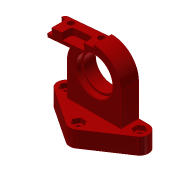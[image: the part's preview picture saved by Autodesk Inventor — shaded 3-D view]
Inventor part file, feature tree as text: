
AUTODESK INVENTOR PART (.ipt)
format: ipt  version: 2015 SP2 (Build 190223200, 223)  size: 307,712 bytes
history: native  units: mm
features: extrude x9, sketch x9, hole x4, projected_geometry x3, fillet x2, other x1, plane x1, chamfer x1
ambient origin geometry x8: Origin, YZ Plane, XZ Plane, XY Plane, X Axis, Y Axis, Z Axis, Center Point
bodies: Body1 (feature_tree)
feature tree (30):
  other  "Sólido1"
  extrude  "Extrusión1"  Depth=5.5mm
  hole  "Agujero1"  [1 undecoded]
  hole  "Agujero2"  [1 undecoded]
  hole  "Agujero3"  [1 undecoded]
  extrude  "Extrusión2"  Depth=10.0mm
  extrude  "Extrusión3"  Depth=6.235mm
  fillet  "Empalme1"  Radius=6.235mm
  hole  "Agujero4"  [1 undecoded]
  extrude  "Extrusión4"  Depth=11.0mm
  extrude  "Extrusión5"  Depth=6.0mm
  extrude  "Extrusión6"  Depth=2.0mm TaperAngle=0.0deg
  extrude  "Extrusión8"  Depth=16.5mm
  fillet  "Empalme2"  Radius=0.872665mm
  sketch  "Boceto8"  dims[d37=6.235mm d38=2.8mm d39=0.0mm]
  plane  "Plano de trabajo1"
  extrude  "Extrusion11"  Depth=6.0mm
  extrude  "Extrusión9"  Depth=29.0mm
  chamfer  "Chaflán3"  Distance=14.9mm
  sketch  "Boceto1"  dims[d0=45.0mm d1=5.5mm]
  sketch  "Boceto3"  dims[d2=5.5mm d3=5.5mm]
  projected_geometry  "Contorno proyectado1"
  sketch  "Boceto4"  dims[d6=10.0mm d7=0.0mm d8=10.0mm d9=10.0mm]
  projected_geometry  "Contorno proyectado2"
  sketch  "Boceto5"  dims[d10=3.75mm d11=6.0mm d12=4.0mm d13=2.0mm d14=90.0deg d15=8.0mm d16=20.594885mm d17=10.0mm d18=10.0mm]
  sketch  "Boceto6"  dims[d19=3.75mm d20=6.0mm d21=4.0mm d22=2.0mm d23=90.0deg d24=8.0mm d25=20.594885mm d26=10.0mm d27=10.0mm]
  sketch  "Boceto7"  dims[d28=3.75mm d29=6.0mm d30=4.0mm d31=2.0mm d32=90.0deg d33=8.0mm d34=20.594885mm d35=6.235mm d36=6.235mm]
  sketch  "Boceto9"  dims[d40=33.0mm d41=11.0mm]
  projected_geometry  "Contorno proyectado3"
  sketch  "Boceto10"  dims[d42=6.0mm d43=6.0mm d44=36.5mm d45=0.0mm d46=16.5mm d68=10.0mm d69=10.0mm d49=22.5mm d50=6.0mm d51=4.0mm d52=2.0mm d53=90.0deg d54=8.0mm d55=20.594885mm d56=0.872665mm d57=6.0mm d58=29.0mm d59=14.9mm d60=11.0mm d61=0.0mm d64=3.0mm d65=11.0mm d66=0.0mm d67=90.0deg d71=7.5mm d72=0.0mm d81=3.0mm d82=9.0mm d83=6.0mm d86=13.5mm d87=4.0mm d88=0.0mm d89=2.0mm d90=-2.5mm d91=6.235mm d92=6.235mm d95=4.0mm d96=0.0mm d98=15.0mm d99=0.5mm d100=2.0mm d101=30.0deg d103=3.75mm d104=3.75mm d107=20.0mm d108=3.0mm d109=18.75mm d111=6.75mm d112=10.0mm d113=0.0mm d114=1.5mm d115=1.0mm d116=120.0deg d117=9.25mm d118=2.0mm d119=2.0mm]
note: 4 required parameter values undecoded (feature->parameter linkage not recoverable at this tier; creation-order binding heuristic only, values carry confidence <= 0.55)
